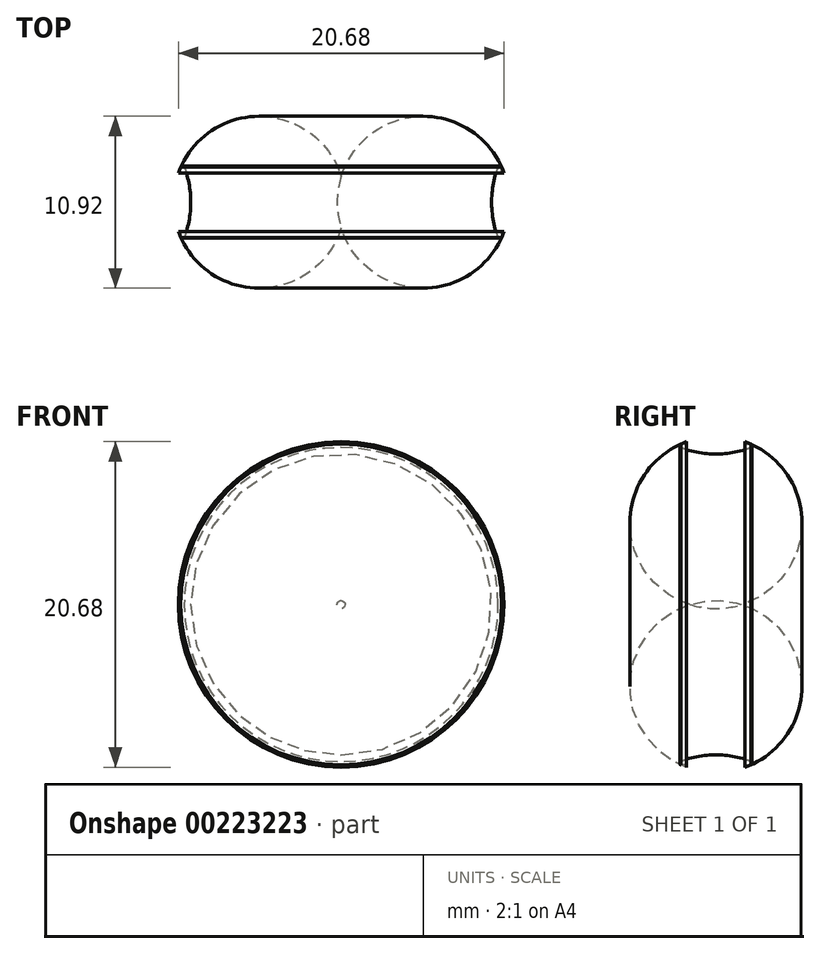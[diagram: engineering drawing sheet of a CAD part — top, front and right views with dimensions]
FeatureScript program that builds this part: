
annotation { "Feature Type Name" : "Feature", "Feature Type Description" : "" }
export const myFeature = defineFeature(function(context is Context, id is Id, definition is map)
    precondition{}
    {
        {
            var Q0;
            Q0=qCreatedBy(makeId("Right.planeOp"),FACE);
            var sketch = newSketch(context, id + "F0", { "sketchPlane" : qUnion([Q0])});
            skLineSegment(sketch, "E0", {"start": v(-5.25, 0) * mm, "end": v(5.47, 0) * mm, "construction": true});
            skLineSegment(sketch, "E1", {"start": v(-2.5, 10.06) * mm, "end": v(2.5, 10.06) * mm, "construction": true});
            skPoint(sketch, "E2.visualSharp", {"position": v(-2.5, 10.06) * mm});
            skLineSegment(sketch, "E3", {"start": v(0, 10.06) * mm, "end": v(0, 12.06) * mm, "construction": true});
            skArc(sketch, "E4", {"start": v(2.29, 10.16) * mm, "mid": v(0, 10.66) * mm, "end": v(-2.29, 10.16) * mm});
            skArc(sketch, "E5", {"start": v(-2.29, 9.97) * mm, "mid": v(0, 9.56) * mm, "end": v(2.29, 9.97) * mm});
            skLineSegment(sketch, "E6", {"start": v(-2.29, 9.97) * mm, "end": v(-2.29, 10.16) * mm});
            skLineSegment(sketch, "E7", {"start": v(2.29, 9.97) * mm, "end": v(2.29, 10.16) * mm});
            skSolve(sketch);
        }
        {
            var Q0;
            Q0 = qSketchRegion(id + "F0", true);
            var Q1;
            Q1=sQuery(id+"F0.wireOp",EDGE,"E0");
            revolve(context, id + "F1", {"entities" : qUnion([Q0]), "axis" : qUnion([Q1]), "revolveType" : RevolveType.FULL});
        }
        {
            var Q0;
            Q0=qCreatedBy(makeId("Right.planeOp"),FACE);
            var sketch = newSketch(context, id + "F2", { "sketchPlane" : qUnion([Q0])});
            skPoint(sketch, "E8", {"position": v(-2.29, 10.16) * mm});
            skLineSegment(sketch, "E9", {"start": v(-2.29, 10.16) * mm, "end": v(-1.85, 11.22) * mm});
            skLineSegment(sketch, "E10", {"start": v(-1.85, 11.22) * mm, "end": v(-1.86, 10.31) * mm});
            skLineSegment(sketch, "E11", {"start": v(-1.99, 10.19) * mm, "end": v(-2.27, 10.19) * mm});
            skLineSegment(sketch, "E12", {"start": v(0, 10.79) * mm, "end": v(0, 10.12) * mm, "construction": true});
            skPoint(sketch, "E13.visualSharp", {"position": v(-1.86, 10.19) * mm});
            skArc(sketch, "E13.filletArc", {"start": v(-1.99, 10.19) * mm, "mid": v(-1.9, 10.22) * mm, "end": v(-1.86, 10.31) * mm});
            skLineSegment(sketch, "E14.MirrorCS", {"start": v(1.99, 10.19) * mm, "end": v(2.27, 10.19) * mm});
            skLineSegment(sketch, "E15.MirrorCS", {"start": v(2.29, 10.16) * mm, "end": v(1.85, 11.22) * mm});
            skLineSegment(sketch, "E16.MirrorCS", {"start": v(1.85, 11.22) * mm, "end": v(1.86, 10.31) * mm});
            skPoint(sketch, "E17.MirrorP", {"position": v(1.86, 10.19) * mm});
            skPoint(sketch, "E18.MirrorP", {"position": v(2.29, 10.16) * mm});
            skArc(sketch, "E19.MirrorCS", {"start": v(1.99, 10.19) * mm, "mid": v(1.9, 10.22) * mm, "end": v(1.86, 10.31) * mm});
            skSolve(sketch);
        }
        {
            var Q0;
            {var subQ0=sQuery(id+"F2.wireOp",EDGE,"E10");Q0=makeQuery(id+"F2.imprint","IMPRINT",FACE,{"disambiguationData":[TD([[makeQuery(id+"F2.imprint","IMPRINT",EDGE,{"derivedFrom":subQ0}),-1.0]])]});}
            var Q1;
            {var subQ0=sQuery(id+"F2.wireOp",EDGE,"E14.MirrorCS");Q1=makeQuery(id+"F2.imprint","IMPRINT",FACE,{"disambiguationData":[TD([[makeQuery(id+"F2.imprint","IMPRINT",EDGE,{"derivedFrom":subQ0}),1.0]])]});}
            var Q2;
            Q2=makeQuery(id+"F1.opRevolve","SWEPT_EDGE",EDGE,{"disambiguationData":[OSD([sQuery(id+"F0.wireOp",EDGE,"E4"),sQuery(id+"F0.wireOp",EDGE,"E6")])]});
            sweep(context, id + "F3", {"operationType" : NewBodyOperationType.REMOVE, "profiles" : qUnion([Q0, Q1]), "path" : qUnion([Q2])});
        }
    });
